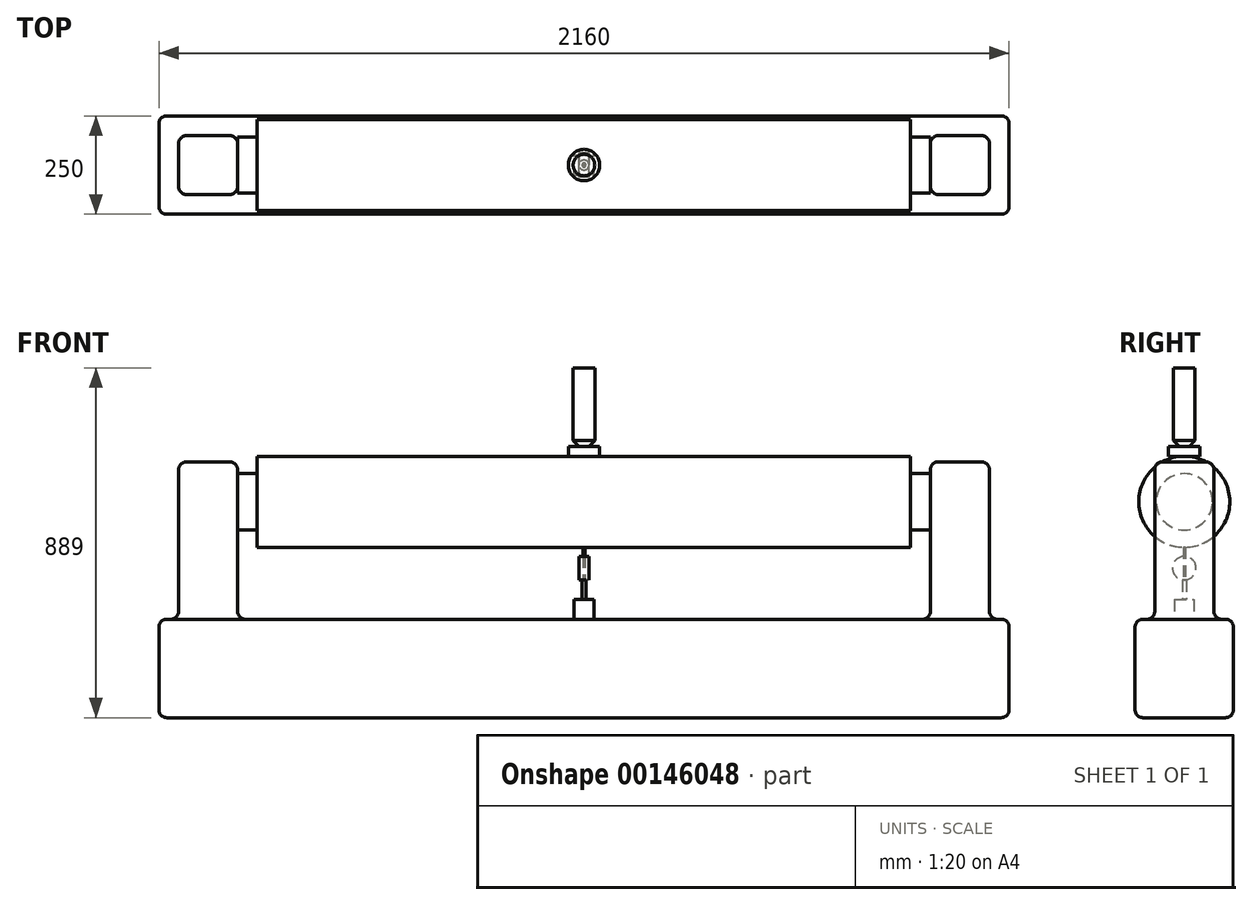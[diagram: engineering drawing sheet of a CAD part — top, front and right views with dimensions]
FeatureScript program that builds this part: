
annotation { "Feature Type Name" : "Feature", "Feature Type Description" : "" }
export const myFeature = defineFeature(function(context is Context, id is Id, definition is map)
    precondition{}
    {
        {
            var Q0;
            Q0=qCreatedBy(makeId("Top.planeOp"),FACE);
            var sketch = newSketch(context, id + "F0", { "sketchPlane" : qUnion([Q0])});
            skLineSegment(sketch, "E0.bottom", {"start": v(1080, -125) * mm, "end": v(-1080, -125) * mm});
            skLineSegment(sketch, "E0.top", {"start": v(1080, 125) * mm, "end": v(-1080, 125) * mm});
            skLineSegment(sketch, "E0.left", {"start": v(1080, -125) * mm, "end": v(1080, 125) * mm});
            skLineSegment(sketch, "E0.right", {"start": v(-1080, -125) * mm, "end": v(-1080, 125) * mm});
            skPoint(sketch, "E0.middle", {"position": v(0, 0) * mm});
            skSolve(sketch);
        }
        {
            var Q0;
            Q0 = qSketchRegion(id + "F0", true);
            extrude(context, id + "F1", {"entities" : qUnion([Q0]), "depth" : 250 * mm});
        }
        {
            var Q0;
            Q0=makeQuery(id+"F1.opExtrude","CAP_FACE",FACE,{"disambiguationData":[OSD([sQuery(id+"F0.wireOp",EDGE,"E0.bottom"),sQuery(id+"F0.wireOp",EDGE,"E0.top"),sQuery(id+"F0.wireOp",EDGE,"E0.left"),sQuery(id+"F0.wireOp",EDGE,"E0.right")])],"isStart":false});
            var sketch = newSketch(context, id + "F2", { "sketchPlane" : qUnion([Q0])});
            skLineSegment(sketch, "E1.bottom", {"start": v(-1030, 75) * mm, "end": v(-880, 75) * mm});
            skLineSegment(sketch, "E1.top", {"start": v(-1030, -75) * mm, "end": v(-880, -75) * mm});
            skLineSegment(sketch, "E1.left", {"start": v(-1030, 75) * mm, "end": v(-1030, -75) * mm});
            skLineSegment(sketch, "E1.right", {"start": v(-880, 75) * mm, "end": v(-880, -75) * mm});
            skLineSegment(sketch, "E2.bottom", {"start": v(880, 75) * mm, "end": v(1030, 75) * mm});
            skLineSegment(sketch, "E2.top", {"start": v(880, -75) * mm, "end": v(1030, -75) * mm});
            skLineSegment(sketch, "E2.left", {"start": v(880, 75) * mm, "end": v(880, -75) * mm});
            skLineSegment(sketch, "E2.right", {"start": v(1030, 75) * mm, "end": v(1030, -75) * mm});
            skLineSegment(sketch, "E3", {"start": v(-1080, 0) * mm, "end": v(-1030, 0) * mm, "construction": true});
            skLineSegment(sketch, "E4", {"start": v(1080, 0) * mm, "end": v(1030, 0) * mm, "construction": true});
            skSolve(sketch);
        }
        {
            var Q0;
            Q0 = qSketchRegion(id + "F2", true);
            extrude(context, id + "F3", {"entities" : qUnion([Q0]), "operationType" : NewBodyOperationType.ADD, "depth" : 400 * mm});
        }
        {
            var Q0;
            Q0=makeQuery(id+"F3.opExtrude","SWEPT_FACE",FACE,{"disambiguationData":[OSD([sQuery(id+"F2.wireOp",EDGE,"E1.right")])]});
            var sketch = newSketch(context, id + "F4", { "sketchPlane" : qUnion([Q0])});
            skCircle(sketch, "E5", {"center": v(0, 548.5) * mm, "radius": 71.5 * mm});
            skPoint(sketch, "E6", {"position": v(0, 650) * mm});
            skSolve(sketch);
        }
        {
            var Q0;
            Q0 = qSketchRegion(id + "F4", true);
            extrude(context, id + "F5", {"entities" : qUnion([Q0]), "depth" : 50 * mm});
        }
        {
            var Q0;
            Q0=makeQuery(id+"F5.opExtrude","SWEPT_BODY",BODY,{"disambiguationData":[OSD([sQuery(id+"F4.wireOp",EDGE,"E5")])]});
            var Q1;
            Q1=qCreatedBy(makeId("Right.planeOp"),FACE);
            mirror(context, id + "F6", {"entities" : qUnion([Q0]), "mirrorPlane" : qUnion([Q1])});
        }
        {
            var Q0;
            Q0=makeQuery(id+"F1.opExtrude","SWEPT_FACE",FACE,{"disambiguationData":[OSD([sQuery(id+"F0.wireOp",EDGE,"E0.bottom")])]});
            var Q1;
            Q1=makeQuery(id+"F1.opExtrude","CAP_FACE",FACE,{"disambiguationData":[OSD([sQuery(id+"F0.wireOp",EDGE,"E0.bottom"),sQuery(id+"F0.wireOp",EDGE,"E0.top"),sQuery(id+"F0.wireOp",EDGE,"E0.left"),sQuery(id+"F0.wireOp",EDGE,"E0.right")])],"isStart":false});
            var Q2;
            Q2=makeQuery(id+"F1.opExtrude","SWEPT_FACE",FACE,{"disambiguationData":[OSD([sQuery(id+"F0.wireOp",EDGE,"E0.top")])]});
            var Q3;
            Q3=makeQuery(id+"F1.opExtrude","CAP_FACE",FACE,{"disambiguationData":[OSD([sQuery(id+"F0.wireOp",EDGE,"E0.bottom"),sQuery(id+"F0.wireOp",EDGE,"E0.top"),sQuery(id+"F0.wireOp",EDGE,"E0.left"),sQuery(id+"F0.wireOp",EDGE,"E0.right")])],"isStart":true});
            var Q4;
            Q4=makeQuery(id+"F3.opExtrude","SWEPT_FACE",FACE,{"disambiguationData":[OSD([sQuery(id+"F2.wireOp",EDGE,"E2.top")])]});
            var Q5;
            Q5=makeQuery(id+"F3.opExtrude","SWEPT_FACE",FACE,{"disambiguationData":[OSD([sQuery(id+"F2.wireOp",EDGE,"E2.right")])]});
            var Q6;
            Q6=makeQuery(id+"F3.opExtrude","SWEPT_FACE",FACE,{"disambiguationData":[OSD([sQuery(id+"F2.wireOp",EDGE,"E2.bottom")])]});
            var Q7;
            Q7=makeQuery(id+"F3.opExtrude","CAP_FACE",FACE,{"disambiguationData":[OSD([sQuery(id+"F2.wireOp",EDGE,"E2.bottom"),sQuery(id+"F2.wireOp",EDGE,"E2.top"),sQuery(id+"F2.wireOp",EDGE,"E2.left"),sQuery(id+"F2.wireOp",EDGE,"E2.right")])],"isStart":false});
            var Q8;
            Q8=makeQuery(id+"F3.opExtrude","SWEPT_FACE",FACE,{"disambiguationData":[OSD([sQuery(id+"F2.wireOp",EDGE,"E1.left")])]});
            var Q9;
            Q9=makeQuery(id+"F3.opExtrude","SWEPT_FACE",FACE,{"disambiguationData":[OSD([sQuery(id+"F2.wireOp",EDGE,"E1.top")])]});
            var Q10;
            Q10=makeQuery(id+"F3.opExtrude","CAP_FACE",FACE,{"disambiguationData":[OSD([sQuery(id+"F2.wireOp",EDGE,"E1.bottom"),sQuery(id+"F2.wireOp",EDGE,"E1.top"),sQuery(id+"F2.wireOp",EDGE,"E1.left"),sQuery(id+"F2.wireOp",EDGE,"E1.right")])],"isStart":false});
            var Q11;
            Q11=makeQuery(id+"F3.opExtrude","SWEPT_FACE",FACE,{"disambiguationData":[OSD([sQuery(id+"F2.wireOp",EDGE,"E1.bottom")])]});
            fillet(context, id + "F7", {"entities" : qUnion([Q0, Q1, Q2, Q3, Q4, Q5, Q6, Q7, Q8, Q9, Q10, Q11]), "radius" : 20 * mm, "tangentPropagation" : true, "allowEdgeOverflow" : false});
        }
        {
            var Q0;
            Q0=makeQuery(id+"F5.opExtrude","CAP_FACE",FACE,{"disambiguationData":[OSD([sQuery(id+"F4.wireOp",EDGE,"E5")])],"isStart":false});
            var sketch = newSketch(context, id + "F8", { "sketchPlane" : qUnion([Q0])});
            skCircle(sketch, "E7", {"center": v(0, 548.5) * mm, "radius": 115.61 * mm});
            skSolve(sketch);
        }
        {
            var Q0;
            Q0 = qSketchRegion(id + "F8", true);
            extrude(context, id + "F9", {"entities" : qUnion([Q0]), "depth" : 1660 * mm});
        }
        {
            var Q0;
            Q0=makeQuery(id+"F1.opExtrude","CAP_FACE",FACE,{"disambiguationData":[OSD([sQuery(id+"F0.wireOp",EDGE,"E0.bottom"),sQuery(id+"F0.wireOp",EDGE,"E0.top"),sQuery(id+"F0.wireOp",EDGE,"E0.left"),sQuery(id+"F0.wireOp",EDGE,"E0.right")])],"isStart":false});
            var sketch = newSketch(context, id + "F10", { "sketchPlane" : qUnion([Q0])});
            skLineSegment(sketch, "E8.bottom", {"start": v(-25, -25) * mm, "end": v(25, -25) * mm});
            skLineSegment(sketch, "E8.top", {"start": v(-25, 25) * mm, "end": v(25, 25) * mm});
            skLineSegment(sketch, "E8.left", {"start": v(-25, -25) * mm, "end": v(-25, 25) * mm});
            skLineSegment(sketch, "E8.right", {"start": v(25, -25) * mm, "end": v(25, 25) * mm});
            skPoint(sketch, "E8.middle", {"position": v(0, 0) * mm});
            skSolve(sketch);
        }
        {
            var Q0;
            Q0 = qSketchRegion(id + "F10", true);
            extrude(context, id + "F11", {"entities" : qUnion([Q0]), "depth" : 50 * mm});
        }
        {
            var Q0;
            Q0=makeQuery(id+"F11.opExtrude","CAP_FACE",FACE,{"disambiguationData":[OSD([sQuery(id+"F10.wireOp",EDGE,"E8.bottom"),sQuery(id+"F10.wireOp",EDGE,"E8.top"),sQuery(id+"F10.wireOp",EDGE,"E8.left"),sQuery(id+"F10.wireOp",EDGE,"E8.right")])],"isStart":false});
            var sketch = newSketch(context, id + "F12", { "sketchPlane" : qUnion([Q0])});
            skCircle(sketch, "E9", {"center": v(0, 0) * mm, "radius": 5 * mm});
            skSolve(sketch);
        }
        {
            var Q0;
            Q0 = qSketchRegion(id + "F12", true);
            extrude(context, id + "F13", {"entities" : qUnion([Q0]), "depth" : 50 * mm});
        }
        {
            var Q0;
            Q0=makeQuery(id+"F1.opExtrude","SWEPT_FACE",FACE,{"disambiguationData":[OSD([sQuery(id+"F0.wireOp",EDGE,"E0.left")])]});
            cPlane(context, id + "F14", {"entities" : qUnion([Q0]), "cplaneType" : CPlaneType.OFFSET, "offset" : (2160 / 2) * mm, "oppositeDirection" : true, "width" : 150 * mm, "height" : 150 * mm});
        }
        {
            var Q0;
            Q0=qCreatedBy(id+"F14.planeOp",FACE);
            var sketch = newSketch(context, id + "F15", { "sketchPlane" : qUnion([Q0])});
            skCircle(sketch, "E10", {"center": v(0, 380) * mm, "radius": 30 * mm});
            skSolve(sketch);
        }
        {
            var Q0;
            Q0 = qSketchRegion(id + "F15", true);
            extrude(context, id + "F16", {"entities" : qUnion([Q0]), "operationType" : NewBodyOperationType.ADD, "endBound" : BoundingType.SYMMETRIC, "depth" : 25 * mm});
        }
        {
            var Q0;
            Q0=makeQuery(id+"F13.opExtrude","CAP_FACE",FACE,{"disambiguationData":[OSD([sQuery(id+"F12.wireOp",EDGE,"E9")])],"isStart":false});
            var sketch = newSketch(context, id + "F17", { "sketchPlane" : qUnion([Q0])});
            skCircle(sketch, "E11", {"center": v(0, 0) * mm, "radius": 2.5 * mm});
            skSolve(sketch);
        }
        {
            var Q0;
            Q0 = qSketchRegion(id + "F17", true);
            var Q1;
            Q1=makeQuery(id+"F9.opExtrude","SWEPT_BODY",BODY,{"disambiguationData":[OSD([sQuery(id+"F8.wireOp",EDGE,"E7")])]});
            extrude(context, id + "F18", {"entities" : qUnion([Q0]), "endBound" : BoundingType.UP_TO_BODY, "endBoundEntityBody" : qUnion([Q1]), "depth" : 25 * mm});
        }
        {
            var Q0;
            Q0=makeQuery(id+"F3.opExtrude","CAP_FACE",FACE,{"disambiguationData":[OSD([sQuery(id+"F2.wireOp",EDGE,"E2.bottom"),sQuery(id+"F2.wireOp",EDGE,"E2.top"),sQuery(id+"F2.wireOp",EDGE,"E2.left"),sQuery(id+"F2.wireOp",EDGE,"E2.right")])],"isStart":false});
            cPlane(context, id + "F19", {"entities" : qUnion([Q0]), "cplaneType" : CPlaneType.OFFSET, "offset" : 14 * mm, "width" : 150 * mm, "height" : 150 * mm});
        }
        {
            var Q0;
            Q0=qCreatedBy(id+"F19.planeOp",FACE);
            var sketch = newSketch(context, id + "F20", { "sketchPlane" : qUnion([Q0])});
            skCircle(sketch, "E12", {"center": v(0, 0) * mm, "radius": 40 * mm});
            skSolve(sketch);
        }
        {
            var Q0;
            Q0 = qSketchRegion(id + "F20", true);
            extrude(context, id + "F21", {"entities" : qUnion([Q0]), "depth" : 25 * mm});
        }
        {
            var Q0;
            Q0=makeQuery(id+"F21.opExtrude","CAP_FACE",FACE,{"disambiguationData":[OSD([sQuery(id+"F20.wireOp",EDGE,"E12")])],"isStart":false});
            var sketch = newSketch(context, id + "F22", { "sketchPlane" : qUnion([Q0])});
            skCircle(sketch, "E13", {"center": v(0, 0) * mm, "radius": 27.5 * mm});
            skSolve(sketch);
        }
        {
            var Q0;
            Q0 = qSketchRegion(id + "F22", true);
            extrude(context, id + "F23", {"entities" : qUnion([Q0]), "depth" : 200 * mm});
        }
        {
            var Q0;
            Q0=makeQuery(id+"F23.opExtrude","CAP_EDGE",EDGE,{"disambiguationData":[OSD([sQuery(id+"F22.wireOp",EDGE,"E13")])],"isStart":true});
            chamfer(context, id + "F24", {"entities" : qUnion([Q0]), "width" : 15 * mm, "tangentPropagation" : true});
        }
    });
